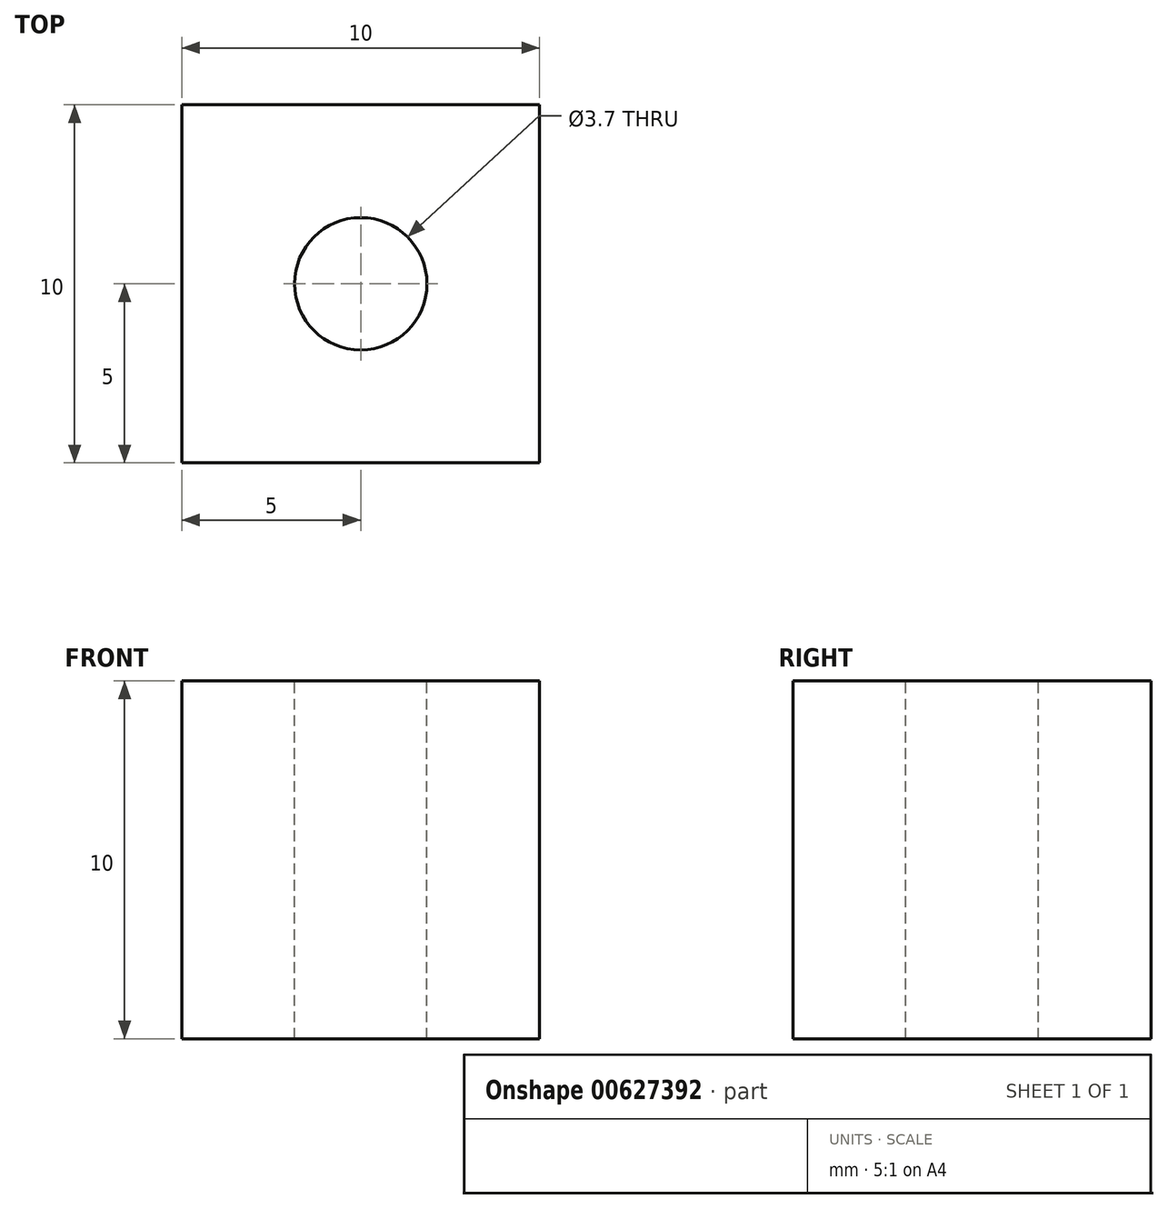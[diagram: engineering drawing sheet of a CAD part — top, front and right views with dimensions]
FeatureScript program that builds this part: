
annotation { "Feature Type Name" : "Feature", "Feature Type Description" : "" }
export const myFeature = defineFeature(function(context is Context, id is Id, definition is map)
    precondition{}
    {
        {
            var Q0;
            Q0=qCreatedBy(makeId("Top.planeOp"),FACE);
            var sketch = newSketch(context, id + "F0", { "sketchPlane" : qUnion([Q0])});
            skLineSegment(sketch, "E0.bottom", {"start": v(5, -5) * mm, "end": v(-5, -5) * mm});
            skLineSegment(sketch, "E0.top", {"start": v(5, 5) * mm, "end": v(-5, 5) * mm});
            skLineSegment(sketch, "E0.left", {"start": v(5, -5) * mm, "end": v(5, 5) * mm});
            skLineSegment(sketch, "E0.right", {"start": v(-5, -5) * mm, "end": v(-5, 5) * mm});
            skPoint(sketch, "E0.middle", {"position": v(0, 0) * mm});
            skSolve(sketch);
        }
        {
            var Q0;
            Q0 = qSketchRegion(id + "F0", true);
            extrude(context, id + "F1", {"entities" : qUnion([Q0]), "depth" : 10 * mm, "offsetDistance" : 25 * mm});
        }
        {
            var Q0;
            Q0=makeQuery(id+"F1.opExtrude","CAP_FACE",FACE,{"disambiguationData":[OSD([sQuery(id+"F0.wireOp",EDGE,"E0.bottom"),sQuery(id+"F0.wireOp",EDGE,"E0.top"),sQuery(id+"F0.wireOp",EDGE,"E0.left"),sQuery(id+"F0.wireOp",EDGE,"E0.right")])],"isStart":false});
            var sketch = newSketch(context, id + "F2", { "sketchPlane" : qUnion([Q0])});
            skPoint(sketch, "E1", {"position": v(0, 0) * mm});
            skSolve(sketch);
        }
        {
            var Q0;
            Q0=sQuery(id+"F2.wireOp",VERTEX,"E1");
            var Q1;
            Q1=makeQuery(id+"F1.opExtrude","SWEPT_BODY",BODY,{"disambiguationData":[OSD([sQuery(id+"F0.wireOp",EDGE,"E0.bottom"),sQuery(id+"F0.wireOp",EDGE,"E0.top"),sQuery(id+"F0.wireOp",EDGE,"E0.left"),sQuery(id+"F0.wireOp",EDGE,"E0.right")])]});
            hole(context, id + "F3", {"style" : HoleStyle.SIMPLE, "endStyle" : HoleEndStyle.BLIND, "holeDiameter" : 3.7 * mm, "majorDiameter" : 5 * mm, "holeDepth" : 20 * mm, "isTappedThrough" : true, "tappedDepth" : 12 * mm, "tapClearance" : 3, "locations" : qUnion([Q0]), "scope" : qUnion([Q1])});
        }
    });
